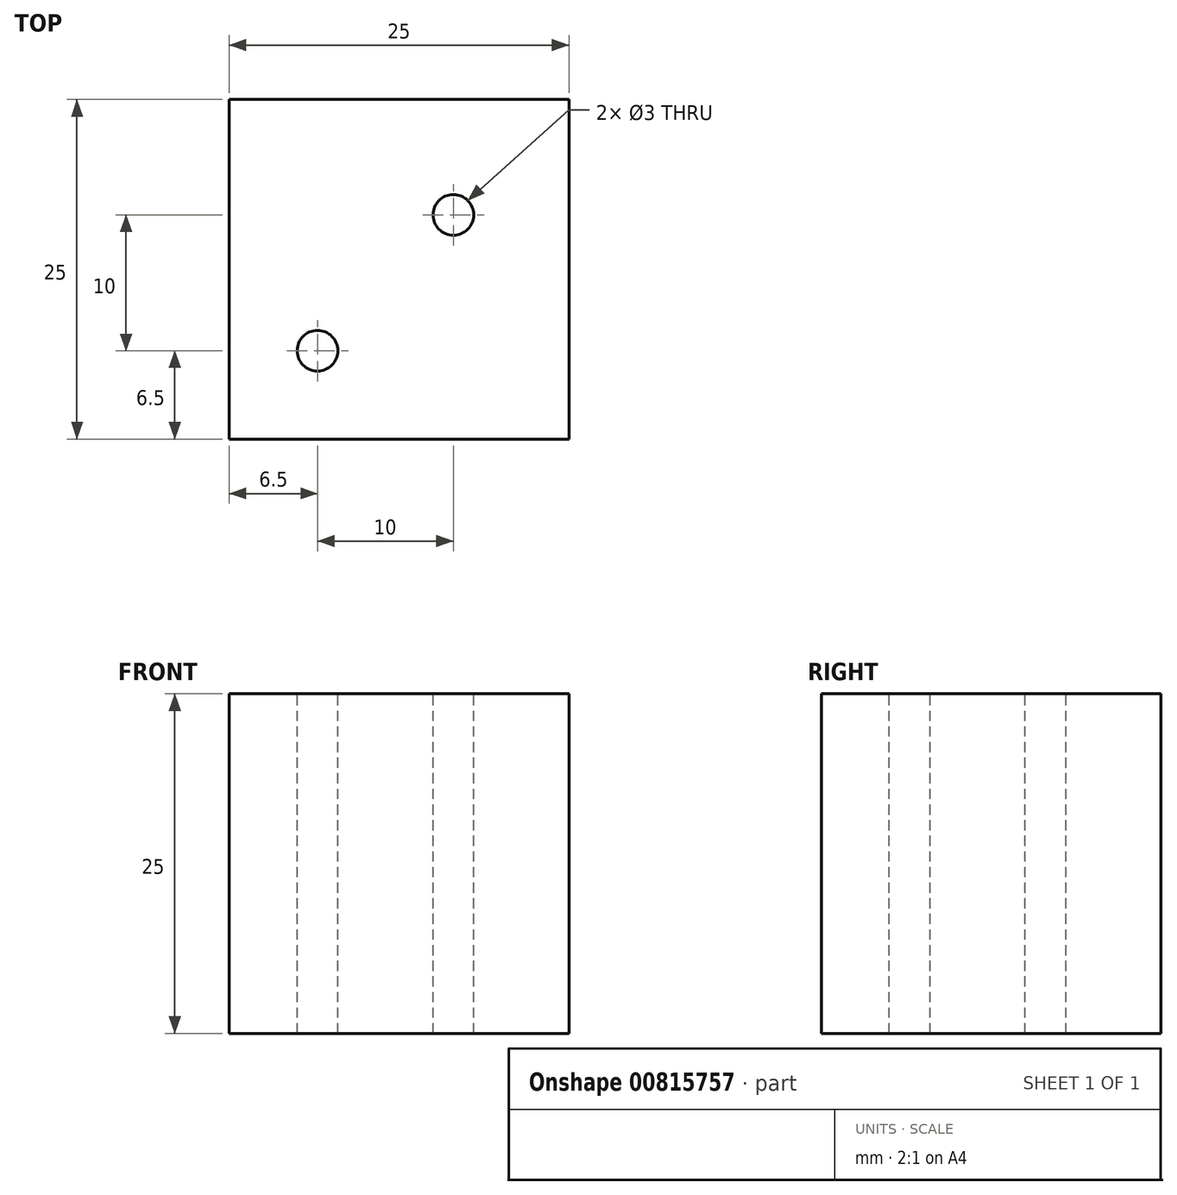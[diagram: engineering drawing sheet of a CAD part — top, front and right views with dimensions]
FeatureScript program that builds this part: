
annotation { "Feature Type Name" : "Feature", "Feature Type Description" : "" }
export const myFeature = defineFeature(function(context is Context, id is Id, definition is map)
    precondition{}
    {
        {
            var Q0;
            Q0=qCreatedBy(makeId("Top.planeOp"),FACE);
            var sketch = newSketch(context, id + "F0", { "sketchPlane" : qUnion([Q0])});
            skLineSegment(sketch, "E0.bottom", {"start": v(12.5, -12.5) * mm, "end": v(-12.5, -12.5) * mm});
            skLineSegment(sketch, "E0.top", {"start": v(12.5, 12.5) * mm, "end": v(-12.5, 12.5) * mm});
            skLineSegment(sketch, "E0.left", {"start": v(12.5, -12.5) * mm, "end": v(12.5, 12.5) * mm});
            skLineSegment(sketch, "E0.right", {"start": v(-12.5, -12.5) * mm, "end": v(-12.5, 12.5) * mm});
            skPoint(sketch, "E0.middle", {"position": v(0, 0) * mm});
            skSolve(sketch);
        }
        {
            var Q0;
            Q0 = qSketchRegion(id + "F0", true);
            extrude(context, id + "F1", {"entities" : qUnion([Q0]), "depth" : 25 * mm, "offsetDistance" : 25 * mm});
        }
        {
            var Q0;
            Q0=makeQuery(id+"F1.opExtrude","CAP_FACE",FACE,{"disambiguationData":[OSD([sQuery(id+"F0.wireOp",EDGE,"E0.bottom"),sQuery(id+"F0.wireOp",EDGE,"E0.top"),sQuery(id+"F0.wireOp",EDGE,"E0.left"),sQuery(id+"F0.wireOp",EDGE,"E0.right")])],"isStart":false});
            var sketch = newSketch(context, id + "F2", { "sketchPlane" : qUnion([Q0])});
            skLineSegment(sketch, "E1.bottom", {"start": v(6, -6) * mm, "end": v(-6, -6) * mm});
            skLineSegment(sketch, "E1.top", {"start": v(6, 6) * mm, "end": v(-6, 6) * mm});
            skLineSegment(sketch, "E1.left", {"start": v(6, -6) * mm, "end": v(6, 6) * mm});
            skLineSegment(sketch, "E1.right", {"start": v(-6, -6) * mm, "end": v(-6, 6) * mm});
            skPoint(sketch, "E1.middle", {"position": v(0, 0) * mm});
            skSolve(sketch);
        }
        {
            var Q0;
            Q0=sQuery(id+"F2.wireOp",VERTEX,"E1.bottom.end");
            var Q1;
            Q1=makeQuery(id+"F1.opExtrude","SWEPT_BODY",BODY,{"disambiguationData":[OSD([sQuery(id+"F0.wireOp",EDGE,"E0.bottom"),sQuery(id+"F0.wireOp",EDGE,"E0.top"),sQuery(id+"F0.wireOp",EDGE,"E0.left"),sQuery(id+"F0.wireOp",EDGE,"E0.right")])]});
            hole(context, id + "F3", {"style" : HoleStyle.SIMPLE, "endStyle" : HoleEndStyle.THROUGH, "holeDiameter" : 3 * mm, "majorDiameter" : 5 * mm, "isTappedThrough" : true, "tappedDepth" : 12 * mm, "tapClearance" : 3, "locations" : qUnion([Q0]), "scope" : qUnion([Q1])});
        }
        {
            var Q0;
            Q0=makeQuery(id+"F1.opExtrude","CAP_FACE",FACE,{"disambiguationData":[OSD([sQuery(id+"F0.wireOp",EDGE,"E0.bottom"),sQuery(id+"F0.wireOp",EDGE,"E0.top"),sQuery(id+"F0.wireOp",EDGE,"E0.left"),sQuery(id+"F0.wireOp",EDGE,"E0.right")])],"isStart":false});
            var sketch = newSketch(context, id + "F4", { "sketchPlane" : qUnion([Q0])});
            skLineSegment(sketch, "E2.bottom", {"start": v(4, -4) * mm, "end": v(-4, -4) * mm});
            skLineSegment(sketch, "E2.top", {"start": v(4, 4) * mm, "end": v(-4, 4) * mm});
            skLineSegment(sketch, "E2.left", {"start": v(4, -4) * mm, "end": v(4, 4) * mm});
            skLineSegment(sketch, "E2.right", {"start": v(-4, -4) * mm, "end": v(-4, 4) * mm});
            skPoint(sketch, "E2.middle", {"position": v(0, 0) * mm});
            skSolve(sketch);
        }
        {
            var Q0;
            Q0=sQuery(id+"F4.wireOp",VERTEX,"E2.top.start");
            var Q1;
            Q1=makeQuery(id+"F1.opExtrude","SWEPT_BODY",BODY,{"disambiguationData":[OSD([sQuery(id+"F0.wireOp",EDGE,"E0.bottom"),sQuery(id+"F0.wireOp",EDGE,"E0.top"),sQuery(id+"F0.wireOp",EDGE,"E0.left"),sQuery(id+"F0.wireOp",EDGE,"E0.right")])]});
            hole(context, id + "F5", {"style" : HoleStyle.SIMPLE, "endStyle" : HoleEndStyle.THROUGH, "holeDiameter" : 3 * mm, "majorDiameter" : 5 * mm, "isTappedThrough" : true, "tappedDepth" : 12 * mm, "tapClearance" : 3, "locations" : qUnion([Q0]), "scope" : qUnion([Q1])});
        }
    });
